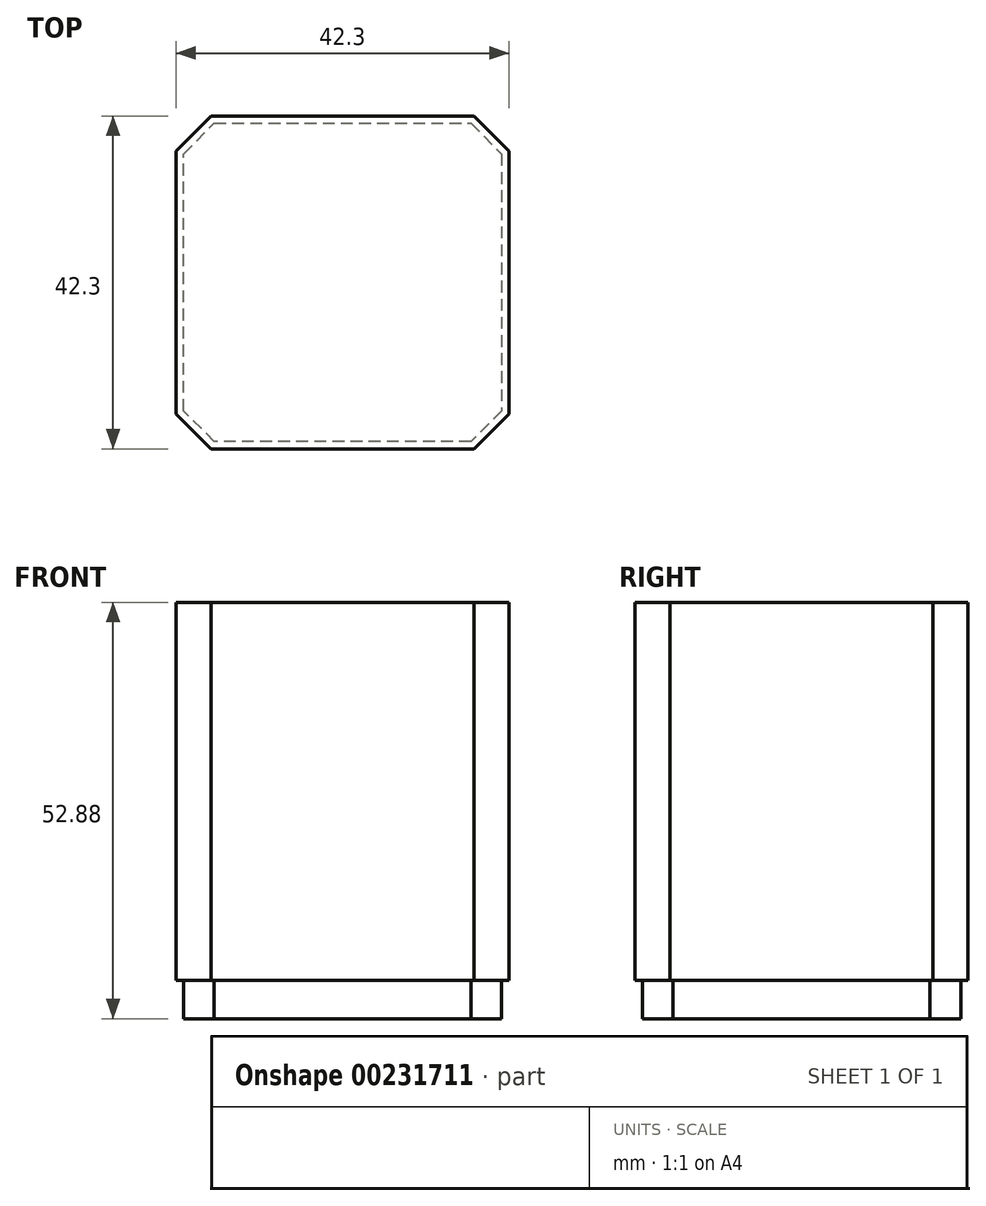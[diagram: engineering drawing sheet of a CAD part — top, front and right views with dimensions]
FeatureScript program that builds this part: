
annotation { "Feature Type Name" : "Feature", "Feature Type Description" : "" }
export const myFeature = defineFeature(function(context is Context, id is Id, definition is map)
    precondition{}
    {
        {
            var Q0;
            Q0=qCreatedBy(makeId("Top.planeOp"),FACE);
            var sketch = newSketch(context, id + "F0", { "sketchPlane" : qUnion([Q0])});
            skLineSegment(sketch, "E0.bottom", {"start": v(21.15, 21.15) * mm, "end": v(-21.15, 21.15) * mm});
            skLineSegment(sketch, "E0.top", {"start": v(21.15, -21.15) * mm, "end": v(-21.15, -21.15) * mm});
            skLineSegment(sketch, "E0.left", {"start": v(21.15, 21.15) * mm, "end": v(21.15, -21.15) * mm});
            skLineSegment(sketch, "E0.right", {"start": v(-21.15, 21.15) * mm, "end": v(-21.15, -21.15) * mm});
            skPoint(sketch, "E0.middle", {"position": v(0, 0) * mm});
            skSolve(sketch);
        }
        {
            var Q0;
            Q0=makeQuery(id+"F0.imprint","IMPRINT",FACE,{"disambiguationData":[TD([[makeQuery(id+"F0.imprint","IMPRINT",EDGE,{"derivedFrom":sQuery(id+"F0.wireOp",EDGE,"E0.bottom")}),1.0]])]});
            extrude(context, id + "F1", {"entities" : qUnion([Q0]), "depth" : 48 * mm});
        }
        {
            var Q0;
            Q0=makeQuery(id+"F1.opExtrude","SWEPT_EDGE",EDGE,{"disambiguationData":[OSD([sQuery(id+"F0.wireOp",EDGE,"E0.bottom"),sQuery(id+"F0.wireOp",EDGE,"E0.left")])]});
            var Q1;
            Q1=makeQuery(id+"F1.opExtrude","SWEPT_EDGE",EDGE,{"disambiguationData":[OSD([sQuery(id+"F0.wireOp",EDGE,"E0.bottom"),sQuery(id+"F0.wireOp",EDGE,"E0.right")])]});
            var Q2;
            Q2=makeQuery(id+"F1.opExtrude","SWEPT_EDGE",EDGE,{"disambiguationData":[OSD([sQuery(id+"F0.wireOp",EDGE,"E0.top"),sQuery(id+"F0.wireOp",EDGE,"E0.right")])]});
            var Q3;
            Q3=makeQuery(id+"F1.opExtrude","SWEPT_EDGE",EDGE,{"disambiguationData":[OSD([sQuery(id+"F0.wireOp",EDGE,"E0.top"),sQuery(id+"F0.wireOp",EDGE,"E0.left")])]});
            chamfer(context, id + "F2", {"entities" : qUnion([Q0, Q1, Q2, Q3]), "width" : 4.44 * mm, "tangentPropagation" : true});
        }
        {
            var Q0;
            Q0=makeQuery(id+"F1.opExtrude","CAP_FACE",FACE,{"disambiguationData":[OSD([sQuery(id+"F0.wireOp",EDGE,"E0.bottom"),sQuery(id+"F0.wireOp",EDGE,"E0.top"),sQuery(id+"F0.wireOp",EDGE,"E0.left"),sQuery(id+"F0.wireOp",EDGE,"E0.right")])],"isStart":true});
            var sketch = newSketch(context, id + "F3", { "sketchPlane" : qUnion([Q0])});
            skLineSegment(sketch, "E1.0", {"start": v(16.32, -20.21) * mm, "end": v(20.21, -16.32) * mm});
            skLineSegment(sketch, "E1.1", {"start": v(-16.32, -20.21) * mm, "end": v(16.32, -20.21) * mm});
            skLineSegment(sketch, "E1.2", {"start": v(20.21, -16.32) * mm, "end": v(20.21, 16.32) * mm});
            skLineSegment(sketch, "E1.3", {"start": v(-20.21, -16.32) * mm, "end": v(-16.32, -20.21) * mm});
            skLineSegment(sketch, "E1.4", {"start": v(20.21, 16.32) * mm, "end": v(16.32, 20.21) * mm});
            skLineSegment(sketch, "E1.5", {"start": v(16.32, 20.21) * mm, "end": v(-16.32, 20.21) * mm});
            skLineSegment(sketch, "E1.6", {"start": v(-16.32, 20.21) * mm, "end": v(-20.21, 16.32) * mm});
            skLineSegment(sketch, "E1.7", {"start": v(-20.21, 16.32) * mm, "end": v(-20.21, -16.32) * mm});
            skSolve(sketch);
        }
        {
            var Q0;
            Q0 = qSketchRegion(id + "F3", true);
            extrude(context, id + "F4", {"entities" : qUnion([Q0]), "operationType" : NewBodyOperationType.ADD, "depth" : 4.88 * mm});
        }
    });
